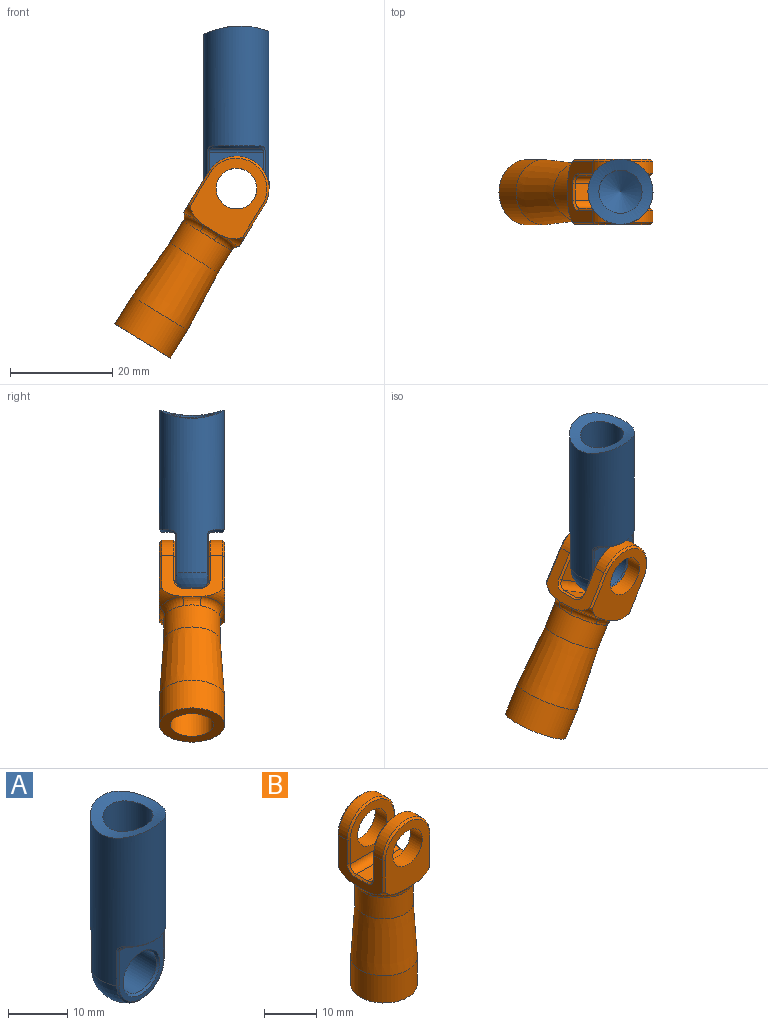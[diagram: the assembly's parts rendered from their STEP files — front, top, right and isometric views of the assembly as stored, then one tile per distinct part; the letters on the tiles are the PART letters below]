
ASSEMBLY  parts=2 mates=1
PART A: 26 faces, bbox 12.7x12.9x38.4 mm
  f0: cylinder r=6.35mm len=31.77mm, axis (0,0,1), area 1014mm2, adj f1,f9,f13,f14,f15,f16,f17,f19
  f1: sphere r=6.35mm, area 118.2mm2, adj f0,f12,f18
  f2: plane 8.87x1.98mm, normal (0,0,-1), area 12.2mm2, adj f7,f23
  f3: plane 12.41x10.53mm, normal (0,1,0), area 58.9mm2, adj f7,f18,f19,f20,f25
  f4: plane 8.87x1.98mm, normal (0,0,-1), area 12.2mm2, adj f8,f17
  f5: plane 12.41x10.53mm, normal (0,-1,0), area 58.9mm2, adj f8,f12,f13,f14,f24
  f6: cylinder r=3.97mm len=7.94mm, axis (0,1,0), area 138.6mm2, adj f24,f25
  f7: cylinder r=0.79mm len=10.53mm, axis (-1,0,0), area 12.1mm2, adj f2,f3,f21,f22
  f8: cylinder r=0.79mm len=10.53mm, axis (-1,0,0), area 12.1mm2, adj f4,f5,f15,f16
  f9: cone r=15.88mm half-angle=2.5deg, axis (-1,0,0), area 73.1mm2, adj f0,f11
  f10: cone r=0mm half-angle=59deg, axis (0,0,1), area 65.2mm2, adj f11
  f11: cylinder r=4.22mm len=17.91mm, axis (0,0,1), area 469.7mm2, adj f9,f10
  f12: cone r=5.62mm half-angle=58.9deg, axis (0,1,0), area 7mm2, adj f1,f5,f13,f14
  f13: plane 7.14x0.35mm, normal (0.52,-0.86,0), area 2.9mm2, adj f0,f5,f12,f15
  f14: plane 7.14x0.35mm, normal (-0.52,-0.86,0), area 2.9mm2, adj f0,f5,f12,f16
  f15: bspline ~1.27x1.19mm, area 0.9mm2, adj f0,f8,f13,f17
  f16: bspline ~1.27x1.19mm, area 0.9mm2, adj f0,f8,f14,f17
  f17: cone r=5.95mm half-angle=45deg, axis (0,0,1), area 5.8mm2, adj f0,f4,f15,f16
  f18: cone r=5.27mm half-angle=58.9deg, axis (0,-1,0), area 7mm2, adj f1,f3,f19,f20
  f19: plane 7.14x0.35mm, normal (0.52,0.86,0), area 2.9mm2, adj f0,f3,f18,f21
  f20: plane 7.14x0.35mm, normal (-0.52,0.86,0), area 2.9mm2, adj f0,f3,f18,f22
  f21: bspline ~1.27x1.19mm, area 0.9mm2, adj f0,f7,f19,f23
  f22: bspline ~1.27x1.19mm, area 0.9mm2, adj f0,f7,f20,f23
  f23: cone r=6.35mm half-angle=45deg, axis (0,0,1), area 5.8mm2, adj f0,f2,f21,f22
  f24: cone r=3.97mm half-angle=45deg, axis (0,-1,0), area 14.7mm2, adj f5,f6
  f25: cone r=4.37mm half-angle=45deg, axis (0,1,0), area 14.7mm2, adj f3,f6
PART B: 49 faces, bbox 18.7x18.7x41.3 mm
  f0: torus R=5.56mm, axis (0,0,1), area 7.9mm2, adj f14,f17,f24,f43
  f1: torus R=5.56mm, axis (0,0,1), area 7.9mm2, adj f14,f16,f20,f41
  f2: torus R=5.56mm, axis (0,0,1), area 7.9mm2, adj f15,f16,f19,f38
  f3: cylinder r=5.56mm len=11.11mm, axis (0,0,1), area 175.3mm2, adj f18,f19,f20,f21,f22,f23,f24,f25
  f4: torus R=5.56mm, axis (0,0,1), area 7.9mm2, adj f15,f17,f23,f40
  f5: plane 11.91x11.51mm, normal (0,-1,0), area 72.3mm2, adj f6,f13,f29,f31,f33
  f6: cylinder r=1.59mm len=11.91mm, axis (-1,0,0), area 29.7mm2, adj f5,f7,f27,f35
  f7: plane 11.91x3.18mm, normal (0,0,1), area 37.8mm2, adj f6,f8,f26,f37
  f8: cylinder r=1.59mm len=11.91mm, axis (1,0,0), area 29.7mm2, adj f7,f9,f28,f36
  f9: plane 11.91x11.51mm, normal (0,1,0), area 72.3mm2, adj f8,f11,f30,f32,f34
  f10: cylinder r=6.35mm len=12.7mm, axis (0,1,0), area 47.5mm2, adj f16,f17,f32,f39
  f11: cylinder r=3.97mm len=7.94mm, axis (0,1,0), area 79.2mm2, adj f9,f15
  f12: cylinder r=6.35mm len=12.7mm, axis (0,1,0), area 47.5mm2, adj f16,f17,f31,f42
  f13: cylinder r=3.97mm len=7.94mm, axis (0,1,0), area 79.2mm2, adj f5,f14
  f14: plane 15.45x11.97mm, normal (0,1,0), area 113.1mm2, adj f0,f1,f13,f22,f41,f42,f43
  f15: plane 15.44x11.97mm, normal (0,-1,0), area 113.1mm2, adj f2,f4,f11,f21,f38,f39,f40
  f16: plane 11.97x9.49mm, normal (-1,0,0), area 54.8mm2, adj f1,f2,f10,f12,f18,f33,f34,f35
  f17: plane 11.97x9.49mm, normal (1,0,0), area 54.8mm2, adj f0,f4,f10,f12,f25,f26,f27,f28
  f18: bspline ~4.78x1.56mm, area 6.2mm2, adj f3,f16,f19,f20
  f19: torus R=7.14mm, axis (0,0,1), area 11.5mm2, adj f2,f3,f18,f21
  f20: torus R=7.14mm, axis (0,0,1), area 11.5mm2, adj f1,f3,f18,f22
  f21: bspline ~4.78x1.56mm, area 6.2mm2, adj f3,f15,f19,f23
  f22: bspline ~4.78x1.56mm, area 6.2mm2, adj f3,f14,f20,f24
  f23: torus R=7.14mm, axis (0,0,1), area 11.5mm2, adj f3,f4,f21,f25
  f24: torus R=7.14mm, axis (0,0,1), area 11.5mm2, adj f0,f3,f22,f25
  f25: bspline ~4.78x1.56mm, area 6.2mm2, adj f3,f17,f23,f24
  f26: plane 3.18x0.4mm, normal (0.71,0,0.71), area 1.8mm2, adj f7,f17,f27,f28
  f27: cone r=1.98mm half-angle=45deg, axis (1,0,0), area 1.6mm2, adj f6,f17,f26,f29
  f28: cone r=1.98mm half-angle=45deg, axis (1,0,0), area 1.6mm2, adj f8,f17,f26,f30
  f29: plane 5.56x0.4mm, normal (0.71,-0.71,0), area 3.1mm2, adj f5,f17,f27,f31
  f30: plane 5.56x0.4mm, normal (0.71,0.71,0), area 3.1mm2, adj f9,f17,f28,f32
  f31: cone r=6.35mm half-angle=45deg, axis (0,1,0), area 10.8mm2, adj f5,f12,f29,f33
  f32: cone r=5.95mm half-angle=45deg, axis (0,-1,0), area 10.8mm2, adj f9,f10,f30,f34
  f33: plane 5.56x0.4mm, normal (-0.71,-0.71,0), area 3.1mm2, adj f5,f16,f31,f35
  f34: plane 5.56x0.4mm, normal (-0.71,0.71,0), area 3.1mm2, adj f9,f16,f32,f36
  f35: cone r=1.98mm half-angle=45deg, axis (-1,0,0), area 1.6mm2, adj f6,f16,f33,f37
  f36: cone r=1.98mm half-angle=45deg, axis (-1,0,0), area 1.6mm2, adj f8,f16,f34,f37
  f37: plane 3.18x0.4mm, normal (-0.71,0,0.71), area 1.8mm2, adj f7,f16,f35,f36
  f38: plane 7.48x0.42mm, normal (-0.71,-0.71,0), area 4.2mm2, adj f2,f15,f16,f39
  f39: cone r=6.35mm half-angle=45deg, axis (0,1,0), area 10.8mm2, adj f10,f15,f38,f40
  f40: plane 7.48x0.42mm, normal (0.71,-0.71,0), area 4.2mm2, adj f4,f15,f17,f39
  f41: plane 7.48x0.42mm, normal (-0.71,0.71,0), area 4.2mm2, adj f1,f14,f16,f42
  f42: cone r=5.95mm half-angle=45deg, axis (0,-1,0), area 10.8mm2, adj f12,f14,f41,f43
  f43: plane 7.48x0.42mm, normal (0.71,0.71,0), area 4.2mm2, adj f0,f14,f17,f42
  f44: cylinder r=6.35mm len=12.7mm, axis (0,0,1), area 253.4mm2, adj f45,f46
  f45: plane 12.7x12.7mm, normal (0,0,-1), area 70.8mm2, adj f44,f48
  f46: cone r=6.35mm half-angle=3.6deg, axis (0,0,-1), area 476mm2, adj f3,f44
  f47: cone r=0mm half-angle=59deg, axis (0,0,-1), area 65.2mm2, adj f48
  f48: cylinder r=4.22mm len=19.05mm, axis (0,0,-1), area 504.7mm2, adj f45,f47
PLACE A at identity
PLACE B rot(axis=(0,1,0),31.6deg) t=(0,0,0)mm
MATE revolute B.f11 <-> A.f12  axis (0,1,0) through (0,-3.18,0)mm
